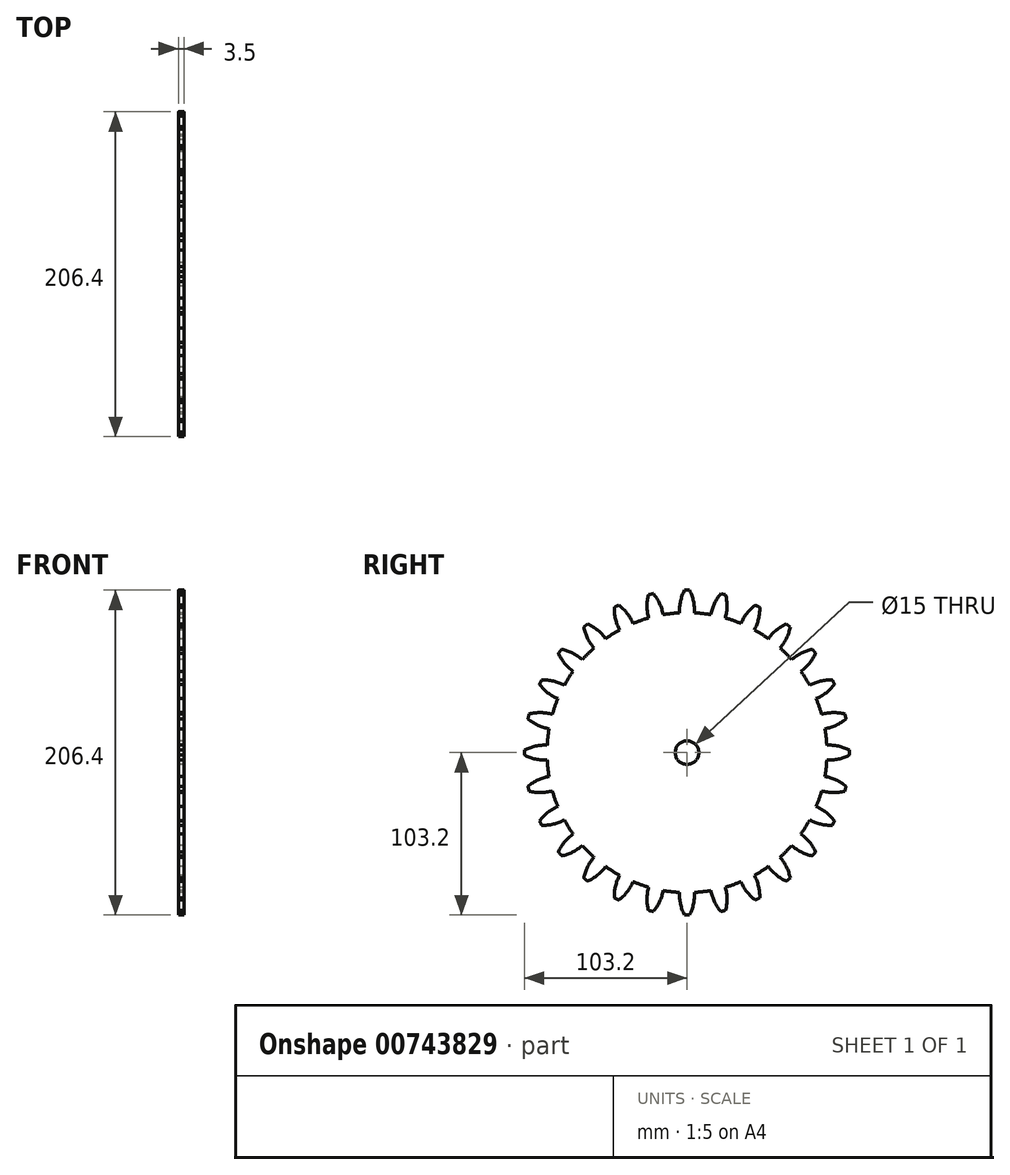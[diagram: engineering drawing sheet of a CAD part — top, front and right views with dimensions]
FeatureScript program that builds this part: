
annotation { "Feature Type Name" : "Feature", "Feature Type Description" : "" }
export const myFeature = defineFeature(function(context is Context, id is Id, definition is map)
    precondition{}
    {
        {
            assignVariable(context, id + "F0", {"name" : "FaceWidth", "anyValue" : 3.5});
        }
        {
            assignVariable(context, id + "F1", {"name" : "NumberTeeth", "anyValue" : 28});
        }
        {
            var Q0;
            Q0=qCreatedBy(makeId("Right.planeOp"),FACE);
            var sketch = newSketch(context, id + "F2", { "sketchPlane" : qUnion([Q0])});
            skCircle(sketch, "E0", {"center": v(0, 0) * mm, "radius": 88.9 * mm});
            skCircle(sketch, "E1", {"center": v(0, 0) * mm, "radius": 7.5 * mm});
            skCircle(sketch, "E2", {"center": v(0, 0) * mm, "radius": 103.2 * mm});
            skPoint(sketch, "E3", {"position": v(0, 88.9) * mm});
            skPoint(sketch, "E4", {"position": v(0, 96.85) * mm});
            skPoint(sketch, "E5", {"position": v(0, 103.2) * mm});
            skLineSegment(sketch, "E6", {"start": v(0, 88.9) * mm, "end": v(0, 96.85) * mm});
            skLineSegment(sketch, "E7", {"start": v(0, 103.2) * mm, "end": v(0, 96.85) * mm});
            skPoint(sketch, "E8", {"position": v(-5.46, 103.06) * mm});
            skLineSegment(sketch, "E9", {"start": v(-5.46, 103.06) * mm, "end": v(0, 0) * mm});
            skArc(sketch, "E10", {"start": v(-1.59, 103.19) * mm, "mid": v(-4.1, 96.19) * mm, "end": v(-4.7, 88.78) * mm});
            skArc(sketch, "E11.MirrorCS", {"start": v(1.59, 103.19) * mm, "mid": v(4.1, 96.19) * mm, "end": v(4.7, 88.78) * mm});
            skLineSegment(sketch, "E12.MirrorCS", {"start": v(5.46, 103.06) * mm, "end": v(0, 0) * mm});
            skPoint(sketch, "E13", {"position": v(-3.98, 96.77) * mm});
            skPoint(sketch, "E14", {"position": v(3.98, 96.77) * mm});
            skArc(sketch, "E15.1.0", {"start": v(-24.5, 100.25) * mm, "mid": v(-25.4, 92.86) * mm, "end": v(-24.34, 85.5) * mm});
            skArc(sketch, "E15.1.1", {"start": v(-21.41, 100.95) * mm, "mid": v(-17.4, 94.7) * mm, "end": v(-15.17, 87.6) * mm});
            skArc(sketch, "E15.2.0", {"start": v(-46.2, 92.28) * mm, "mid": v(-45.44, 84.88) * mm, "end": v(-42.75, 77.94) * mm});
            skArc(sketch, "E15.2.1", {"start": v(-43.34, 93.66) * mm, "mid": v(-38.04, 88.45) * mm, "end": v(-34.28, 82.02) * mm});
            skArc(sketch, "E16.3.3.0", {"start": v(-65.58, 79.69) * mm, "mid": v(-63.18, 72.64) * mm, "end": v(-59.03, 66.48) * mm});
            skArc(sketch, "E16.4.3.0", {"start": v(-63.1, 81.67) * mm, "mid": v(-56.76, 77.76) * mm, "end": v(-51.68, 72.34) * mm});
            skArc(sketch, "E16.3.4.0", {"start": v(-81.67, 63.1) * mm, "mid": v(-77.76, 56.76) * mm, "end": v(-72.34, 51.68) * mm});
            skArc(sketch, "E16.4.4.0", {"start": v(-79.69, 65.58) * mm, "mid": v(-72.64, 63.18) * mm, "end": v(-66.48, 59.03) * mm});
            skArc(sketch, "E16.3.5.0", {"start": v(-93.66, 43.34) * mm, "mid": v(-88.45, 38.04) * mm, "end": v(-82.02, 34.28) * mm});
            skArc(sketch, "E16.4.5.0", {"start": v(-92.28, 46.2) * mm, "mid": v(-84.88, 45.44) * mm, "end": v(-77.94, 42.75) * mm});
            skArc(sketch, "E16.3.6.0", {"start": v(-100.95, 21.41) * mm, "mid": v(-94.7, 17.4) * mm, "end": v(-87.6, 15.17) * mm});
            skArc(sketch, "E16.4.6.0", {"start": v(-100.25, 24.5) * mm, "mid": v(-92.86, 25.4) * mm, "end": v(-85.5, 24.34) * mm});
            skArc(sketch, "E16.3.7.0", {"start": v(-103.19, -1.59) * mm, "mid": v(-96.19, -4.1) * mm, "end": v(-88.78, -4.7) * mm});
            skArc(sketch, "E16.4.7.0", {"start": v(-103.19, 1.59) * mm, "mid": v(-96.19, 4.1) * mm, "end": v(-88.78, 4.7) * mm});
            skArc(sketch, "E16.3.8.0", {"start": v(-100.25, -24.5) * mm, "mid": v(-92.86, -25.4) * mm, "end": v(-85.5, -24.34) * mm});
            skArc(sketch, "E16.4.8.0", {"start": v(-100.95, -21.41) * mm, "mid": v(-94.7, -17.4) * mm, "end": v(-87.6, -15.17) * mm});
            skArc(sketch, "E16.3.9.0", {"start": v(-92.28, -46.2) * mm, "mid": v(-84.88, -45.44) * mm, "end": v(-77.94, -42.75) * mm});
            skArc(sketch, "E16.4.9.0", {"start": v(-93.66, -43.34) * mm, "mid": v(-88.45, -38.04) * mm, "end": v(-82.02, -34.28) * mm});
            skArc(sketch, "E16.3.10.0", {"start": v(-79.69, -65.58) * mm, "mid": v(-72.64, -63.18) * mm, "end": v(-66.48, -59.03) * mm});
            skArc(sketch, "E16.4.10.0", {"start": v(-81.67, -63.1) * mm, "mid": v(-77.76, -56.76) * mm, "end": v(-72.34, -51.68) * mm});
            skArc(sketch, "E16.3.11.0", {"start": v(-63.1, -81.67) * mm, "mid": v(-56.76, -77.76) * mm, "end": v(-51.68, -72.34) * mm});
            skArc(sketch, "E16.4.11.0", {"start": v(-65.58, -79.69) * mm, "mid": v(-63.18, -72.64) * mm, "end": v(-59.03, -66.48) * mm});
            skArc(sketch, "E16.3.12.0", {"start": v(-43.34, -93.66) * mm, "mid": v(-38.04, -88.45) * mm, "end": v(-34.28, -82.02) * mm});
            skArc(sketch, "E16.4.12.0", {"start": v(-46.2, -92.28) * mm, "mid": v(-45.44, -84.88) * mm, "end": v(-42.75, -77.94) * mm});
            skArc(sketch, "E16.3.13.0", {"start": v(-21.41, -100.95) * mm, "mid": v(-17.4, -94.7) * mm, "end": v(-15.17, -87.6) * mm});
            skArc(sketch, "E16.4.13.0", {"start": v(-24.5, -100.25) * mm, "mid": v(-25.4, -92.86) * mm, "end": v(-24.34, -85.5) * mm});
            skArc(sketch, "E16.3.14.0", {"start": v(1.59, -103.19) * mm, "mid": v(4.1, -96.19) * mm, "end": v(4.7, -88.78) * mm});
            skArc(sketch, "E16.4.14.0", {"start": v(-1.59, -103.19) * mm, "mid": v(-4.1, -96.19) * mm, "end": v(-4.7, -88.78) * mm});
            skArc(sketch, "E16.3.15.0", {"start": v(24.5, -100.25) * mm, "mid": v(25.4, -92.86) * mm, "end": v(24.34, -85.5) * mm});
            skArc(sketch, "E16.4.15.0", {"start": v(21.41, -100.95) * mm, "mid": v(17.4, -94.7) * mm, "end": v(15.17, -87.6) * mm});
            skArc(sketch, "E16.3.16.0", {"start": v(46.2, -92.28) * mm, "mid": v(45.44, -84.88) * mm, "end": v(42.75, -77.94) * mm});
            skArc(sketch, "E16.4.16.0", {"start": v(43.34, -93.66) * mm, "mid": v(38.04, -88.45) * mm, "end": v(34.28, -82.02) * mm});
            skArc(sketch, "E16.3.17.0", {"start": v(65.58, -79.69) * mm, "mid": v(63.18, -72.64) * mm, "end": v(59.03, -66.48) * mm});
            skArc(sketch, "E16.4.17.0", {"start": v(63.1, -81.67) * mm, "mid": v(56.76, -77.76) * mm, "end": v(51.68, -72.34) * mm});
            skArc(sketch, "E16.3.18.0", {"start": v(81.67, -63.1) * mm, "mid": v(77.76, -56.76) * mm, "end": v(72.34, -51.68) * mm});
            skArc(sketch, "E16.4.18.0", {"start": v(79.69, -65.58) * mm, "mid": v(72.64, -63.18) * mm, "end": v(66.48, -59.03) * mm});
            skArc(sketch, "E16.3.19.0", {"start": v(93.66, -43.34) * mm, "mid": v(88.45, -38.04) * mm, "end": v(82.02, -34.28) * mm});
            skArc(sketch, "E16.4.19.0", {"start": v(92.28, -46.2) * mm, "mid": v(84.88, -45.44) * mm, "end": v(77.94, -42.75) * mm});
            skArc(sketch, "E16.3.20.0", {"start": v(100.95, -21.41) * mm, "mid": v(94.7, -17.4) * mm, "end": v(87.6, -15.17) * mm});
            skArc(sketch, "E16.4.20.0", {"start": v(100.25, -24.5) * mm, "mid": v(92.86, -25.4) * mm, "end": v(85.5, -24.34) * mm});
            skArc(sketch, "E16.3.21.0", {"start": v(103.19, 1.59) * mm, "mid": v(96.19, 4.1) * mm, "end": v(88.78, 4.7) * mm});
            skArc(sketch, "E16.4.21.0", {"start": v(103.19, -1.59) * mm, "mid": v(96.19, -4.1) * mm, "end": v(88.78, -4.7) * mm});
            skArc(sketch, "E16.3.22.0", {"start": v(100.25, 24.5) * mm, "mid": v(92.86, 25.4) * mm, "end": v(85.5, 24.34) * mm});
            skArc(sketch, "E16.4.22.0", {"start": v(100.95, 21.41) * mm, "mid": v(94.7, 17.4) * mm, "end": v(87.6, 15.17) * mm});
            skArc(sketch, "E16.3.23.0", {"start": v(92.28, 46.2) * mm, "mid": v(84.88, 45.44) * mm, "end": v(77.94, 42.75) * mm});
            skArc(sketch, "E16.4.23.0", {"start": v(93.66, 43.34) * mm, "mid": v(88.45, 38.04) * mm, "end": v(82.02, 34.28) * mm});
            skArc(sketch, "E16.3.24.0", {"start": v(79.69, 65.58) * mm, "mid": v(72.64, 63.18) * mm, "end": v(66.48, 59.03) * mm});
            skArc(sketch, "E16.4.24.0", {"start": v(81.67, 63.1) * mm, "mid": v(77.76, 56.76) * mm, "end": v(72.34, 51.68) * mm});
            skArc(sketch, "E16.3.25.0", {"start": v(63.1, 81.67) * mm, "mid": v(56.76, 77.76) * mm, "end": v(51.68, 72.34) * mm});
            skArc(sketch, "E16.4.25.0", {"start": v(65.58, 79.69) * mm, "mid": v(63.18, 72.64) * mm, "end": v(59.03, 66.48) * mm});
            skArc(sketch, "E16.3.26.0", {"start": v(43.34, 93.66) * mm, "mid": v(38.04, 88.45) * mm, "end": v(34.28, 82.02) * mm});
            skArc(sketch, "E16.4.26.0", {"start": v(46.2, 92.28) * mm, "mid": v(45.44, 84.88) * mm, "end": v(42.75, 77.94) * mm});
            skArc(sketch, "E16.3.27.0", {"start": v(21.41, 100.95) * mm, "mid": v(17.4, 94.7) * mm, "end": v(15.17, 87.6) * mm});
            skArc(sketch, "E16.4.27.0", {"start": v(24.5, 100.25) * mm, "mid": v(25.4, 92.86) * mm, "end": v(24.34, 85.5) * mm});
            skArc(sketch, "E17.trimOffspring", {"start": v(-45.57, 85.46) * mm, "mid": v(-51.53, 82) * mm, "end": v(-57.23, 78.14) * mm});
            skArc(sketch, "E18.trimOffspring", {"start": v(17.66, 95.23) * mm, "mid": v(10.84, 96.24) * mm, "end": v(3.98, 96.77) * mm});
            skArc(sketch, "E19.trimOffspring", {"start": v(38.4, 88.91) * mm, "mid": v(31.99, 91.42) * mm, "end": v(25.4, 93.46) * mm});
            skArc(sketch, "E20.trimOffspring", {"start": v(57.23, 78.14) * mm, "mid": v(51.53, 82) * mm, "end": v(45.57, 85.46) * mm});
            skArc(sketch, "E21.trimOffspring", {"start": v(73.18, 63.44) * mm, "mid": v(68.48, 68.48) * mm, "end": v(63.44, 73.18) * mm});
            skArc(sketch, "E22.trimOffspring", {"start": v(85.46, 45.57) * mm, "mid": v(82, 51.53) * mm, "end": v(78.14, 57.23) * mm});
            skArc(sketch, "E23.trimOffspring", {"start": v(93.46, 25.4) * mm, "mid": v(91.42, 31.99) * mm, "end": v(88.91, 38.4) * mm});
            skArc(sketch, "E24.trimOffspring", {"start": v(96.77, 3.98) * mm, "mid": v(96.24, 10.84) * mm, "end": v(95.23, 17.66) * mm});
            skArc(sketch, "E25.trimOffspring", {"start": v(95.23, -17.66) * mm, "mid": v(96.24, -10.84) * mm, "end": v(96.77, -3.98) * mm});
            skArc(sketch, "E26.trimOffspring", {"start": v(88.91, -38.4) * mm, "mid": v(91.42, -31.99) * mm, "end": v(93.46, -25.4) * mm});
            skArc(sketch, "E27.trimOffspring", {"start": v(78.14, -57.23) * mm, "mid": v(82, -51.53) * mm, "end": v(85.46, -45.57) * mm});
            skArc(sketch, "E28.trimOffspring", {"start": v(63.44, -73.18) * mm, "mid": v(68.48, -68.48) * mm, "end": v(73.18, -63.44) * mm});
            skArc(sketch, "E29.trimOffspring", {"start": v(45.57, -85.46) * mm, "mid": v(51.53, -82) * mm, "end": v(57.23, -78.14) * mm});
            skArc(sketch, "E30.trimOffspring", {"start": v(25.4, -93.46) * mm, "mid": v(31.99, -91.42) * mm, "end": v(38.4, -88.91) * mm});
            skArc(sketch, "E31.trimOffspring", {"start": v(3.98, -96.77) * mm, "mid": v(10.84, -96.24) * mm, "end": v(17.66, -95.23) * mm});
            skArc(sketch, "E32.trimOffspring", {"start": v(-17.66, -95.23) * mm, "mid": v(-10.84, -96.24) * mm, "end": v(-3.98, -96.77) * mm});
            skArc(sketch, "E33.trimOffspring", {"start": v(-38.4, -88.91) * mm, "mid": v(-31.99, -91.42) * mm, "end": v(-25.4, -93.46) * mm});
            skArc(sketch, "E34.trimOffspring", {"start": v(-57.23, -78.14) * mm, "mid": v(-51.53, -82) * mm, "end": v(-45.57, -85.46) * mm});
            skArc(sketch, "E35.trimOffspring", {"start": v(-73.18, -63.44) * mm, "mid": v(-68.48, -68.48) * mm, "end": v(-63.44, -73.18) * mm});
            skArc(sketch, "E36.trimOffspring", {"start": v(-85.46, -45.57) * mm, "mid": v(-82, -51.53) * mm, "end": v(-78.14, -57.23) * mm});
            skArc(sketch, "E37.trimOffspring", {"start": v(-93.46, -25.4) * mm, "mid": v(-91.42, -31.99) * mm, "end": v(-88.91, -38.4) * mm});
            skArc(sketch, "E38.trimOffspring", {"start": v(-96.77, -3.98) * mm, "mid": v(-96.24, -10.84) * mm, "end": v(-95.23, -17.66) * mm});
            skArc(sketch, "E39.trimOffspring", {"start": v(-95.23, 17.66) * mm, "mid": v(-96.24, 10.84) * mm, "end": v(-96.77, 3.98) * mm});
            skArc(sketch, "E40.trimOffspring", {"start": v(-88.91, 38.4) * mm, "mid": v(-91.42, 31.99) * mm, "end": v(-93.46, 25.4) * mm});
            skArc(sketch, "E41.trimOffspring", {"start": v(-78.14, 57.23) * mm, "mid": v(-82, 51.53) * mm, "end": v(-85.46, 45.57) * mm});
            skArc(sketch, "E42.trimOffspring", {"start": v(-63.44, 73.18) * mm, "mid": v(-68.48, 68.48) * mm, "end": v(-73.18, 63.44) * mm});
            skArc(sketch, "E43.trimOffspring", {"start": v(-3.98, 96.77) * mm, "mid": v(-10.84, 96.24) * mm, "end": v(-17.66, 95.23) * mm});
            skSolve(sketch);
        }
        {
            var Q0;
            {var subQ0=sQuery(id+"F2.wireOp",EDGE,"E9");var subQ5=sQuery(id+"F2.wireOp",EDGE,"E1");var subQ7=makeQuery(id+"F2.imprint","INTERSECT",VERTEX,{"derivedFrom":[subQ5,subQ0]});Q0=makeQuery(id+"F2.imprint","IMPRINT",FACE,{"disambiguationData":[TD([[makeQuery(id+"F2.imprint","IMPRINT",EDGE,{"disambiguationData":[TD([[subQ7,-1.0]])],"derivedFrom":subQ5}),-1.0]])]});}
            var Q1;
            {var subQ0=sQuery(id+"F2.wireOp",EDGE,"E9");var subQ3=sQuery(id+"F2.wireOp",EDGE,"E1");var subQ4=makeQuery(id+"F2.imprint","INTERSECT",VERTEX,{"derivedFrom":[subQ3,subQ0]});Q1=makeQuery(id+"F2.imprint","IMPRINT",FACE,{"disambiguationData":[TD([[makeQuery(id+"F2.imprint","IMPRINT",EDGE,{"disambiguationData":[TD([[subQ4,1.0]])],"derivedFrom":subQ3}),-1.0]])]});}
            extrude(context, id + "F3", {"entities" : qUnion([Q0, Q1]), "endBound" : BoundingType.SYMMETRIC, "depth" : (getVariable(context, 'FaceWidth')) * mm, "offsetDistance" : 25.4 * mm});
        }
        {
            var Q0;
            {var subQ0=sQuery(id+"F2.wireOp",EDGE,"E6");Q0=makeQuery(id+"F2.imprint","IMPRINT",FACE,{"disambiguationData":[TD([[makeQuery(id+"F2.imprint","IMPRINT",EDGE,{"derivedFrom":subQ0}),1.0]])]});}
            var Q1;
            {var subQ1=sQuery(id+"F2.wireOp",EDGE,"E6");Q1=makeQuery(id+"F2.imprint","IMPRINT",FACE,{"disambiguationData":[TD([[makeQuery(id+"F2.imprint","IMPRINT",EDGE,{"derivedFrom":subQ1}),-1.0]])]});}
            extrude(context, id + "F4", {"entities" : qUnion([Q0, Q1]), "endBound" : BoundingType.SYMMETRIC, "depth" : (getVariable(context, 'FaceWidth')) * mm, "offsetDistance" : 25.4 * mm});
        }
        {
            var Q0;
            Q0=makeQuery(id+"F4.opExtrude","SWEPT_BODY",BODY,{"disambiguationData":[OSD([sQuery(id+"F2.wireOp",EDGE,"E0"),sQuery(id+"F2.wireOp",EDGE,"E2"),sQuery(id+"F2.wireOp",EDGE,"E10"),sQuery(id+"F2.wireOp",EDGE,"E11.MirrorCS")])]});
            var Q1;
            Q1=makeQuery(id+"F3.opExtrude","SWEPT_FACE",FACE,{"disambiguationData":[OSD([sQuery(id+"F2.wireOp",EDGE,"E1")])]});
            circularPattern(context, id + "F5", {"operationType" : NewBodyOperationType.ADD, "entities" : qUnion([Q0]), "axis" : qUnion([Q1]), "angle" : 360 * degree, "instanceCount" : getVariable(context, 'NumberTeeth'), "equalSpace" : true});
        }
    });
